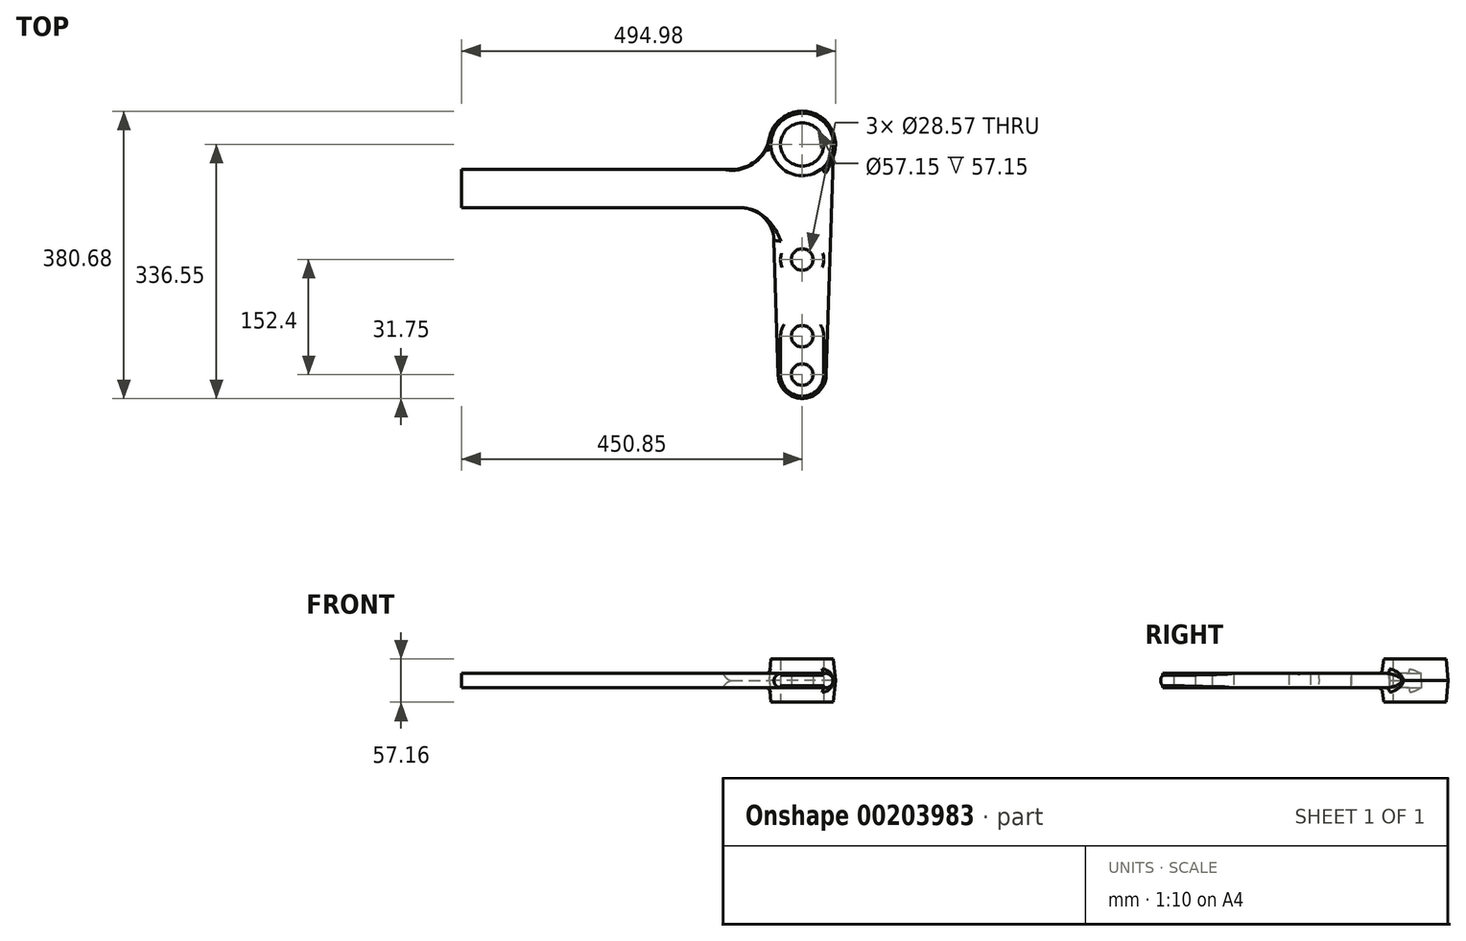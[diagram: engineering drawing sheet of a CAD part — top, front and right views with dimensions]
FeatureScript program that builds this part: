
annotation { "Feature Type Name" : "Feature", "Feature Type Description" : "" }
export const myFeature = defineFeature(function(context is Context, id is Id, definition is map)
    precondition{}
    {
        {
            var Q0;
            Q0=qCreatedBy(makeId("Top.planeOp"),FACE);
            var sketch = newSketch(context, id + "F0", { "sketchPlane" : qUnion([Q0])});
            skLineSegment(sketch, "E0", {"start": v(0, 0) * mm, "end": v(0, -304.8) * mm, "construction": true});
            skPoint(sketch, "E1", {"position": v(0, -254) * mm});
            skPoint(sketch, "E2", {"position": v(0, -152.4) * mm});
            skArc(sketch, "E3", {"start": v(-31.73, -305.8) * mm, "mid": v(0, -336.55) * mm, "end": v(31.73, -305.8) * mm});
            skLineSegment(sketch, "E4", {"start": v(-41.38, -1.31) * mm, "end": v(-31.73, -305.8) * mm});
            skLineSegment(sketch, "E5", {"start": v(41.38, -1.31) * mm, "end": v(31.73, -305.8) * mm});
            skCircle(sketch, "E6.converted", {"center": v(0, 0) * mm, "radius": 41.4 * mm});
            skArc(sketch, "E7", {"start": v(-28.58, -304.8) * mm, "mid": v(0, -333.38) * mm, "end": v(28.58, -304.8) * mm});
            skArc(sketch, "E8", {"start": v(28.58, -254) * mm, "mid": v(0, -225.42) * mm, "end": v(-28.57, -254) * mm});
            skCircle(sketch, "E9", {"center": v(0, -152.4) * mm, "radius": 28.58 * mm});
            skLineSegment(sketch, "E10", {"start": v(-28.57, -254) * mm, "end": v(-28.57, -304.8) * mm});
            skLineSegment(sketch, "E11", {"start": v(28.58, -254) * mm, "end": v(28.58, -304.8) * mm});
            skCircle(sketch, "E12", {"center": v(0, -304.8) * mm, "radius": 14.29 * mm});
            skCircle(sketch, "E13", {"center": v(0, -254) * mm, "radius": 14.29 * mm});
            skCircle(sketch, "E14", {"center": v(0, -152.4) * mm, "radius": 14.29 * mm});
            skCircle(sketch, "E15", {"center": v(0, 0) * mm, "radius": 28.58 * mm});
            skCircle(sketch, "E16.converted", {"center": v(0, 0) * mm, "radius": 44.45 * mm});
            skLineSegment(sketch, "E17", {"start": v(0, 0) * mm, "end": v(-450.85, -1.31) * mm, "construction": true});
            skLineSegment(sketch, "E18", {"start": v(-450.85, -33.06) * mm, "end": v(-40.38, -33.06) * mm});
            skLineSegment(sketch, "E19", {"start": v(-450.85, -83.86) * mm, "end": v(-38.77, -83.86) * mm});
            skLineSegment(sketch, "E20", {"start": v(-450.85, -1.31) * mm, "end": v(-450.85, -33.06) * mm, "construction": true});
            skLineSegment(sketch, "E21", {"start": v(-450.85, -33.06) * mm, "end": v(-450.85, -83.86) * mm});
            skArc(sketch, "E22", {"start": v(-93.58, -33.06) * mm, "mid": v(-61.18, -21.38) * mm, "end": v(-43.67, 8.28) * mm});
            skLineSegment(sketch, "E23", {"start": v(-43.67, 8.28) * mm, "end": v(-40.57, 8.28) * mm});
            skArc(sketch, "E24", {"start": v(-37.4, -126.9) * mm, "mid": v(-50.9, -96.39) * mm, "end": v(-81.83, -83.86) * mm});
            skSolve(sketch);
        }
        {
            var Q0;
            Q0=makeQuery(id+"F0.imprint","IMPRINT",FACE,{"disambiguationData":[TD([[makeQuery(id+"F0.imprint","IMPRINT",EDGE,{"derivedFrom":sQuery(id+"F0.wireOp",EDGE,"E3")}),1.0]])]});
            var Q1;
            {var subQ0=sQuery(id+"F0.wireOp",EDGE,"lDwGXFCf-zemv-MaXU-C33S-ghSfjxrpF6rd");Q1=makeQuery(id+"F0.imprint","IMPRINT",FACE,{"disambiguationData":[TD([[makeQuery(id+"F0.imprint","IMPRINT",EDGE,{"derivedFrom":subQ0}),1.0]])]});}
            var Q2;
            {var subQ0=sQuery(id+"F0.wireOp",EDGE,"E6.converted");var subQ1=sQuery(id+"F0.wireOp",EDGE,"E4");var subQ2=makeQuery(id+"F0.imprint","INTERSECT",VERTEX,{"derivedFrom":[subQ1,subQ0]});Q2=makeQuery(id+"F0.imprint","IMPRINT",FACE,{"disambiguationData":[TD([[makeQuery(id+"F0.imprint","IMPRINT",EDGE,{"disambiguationData":[TD([[subQ2,-1.0]])],"derivedFrom":subQ1}),1.0]])]});}
            extrude(context, id + "F1", {"entities" : qUnion([Q0, Q1, Q2]), "depth" : 9.52 * mm});
        }
        {
            var Q0;
            {var subQ5=sQuery(id+"F0.wireOp",EDGE,"E23");Q0=makeQuery(id+"F0.imprint","IMPRINT",FACE,{"disambiguationData":[TD([[makeQuery(id+"F0.imprint","IMPRINT",EDGE,{"derivedFrom":subQ5}),-1.0]])]});}
            var Q1;
            Q1=makeQuery(id+"F0.imprint","IMPRINT",FACE,{"disambiguationData":[TD([[makeQuery(id+"F0.imprint","IMPRINT",EDGE,{"derivedFrom":sQuery(id+"F0.wireOp",EDGE,"E18")}),-1.0]])]});
            var Q2;
            {var subQ5=sQuery(id+"F0.wireOp",EDGE,"E22");Q2=makeQuery(id+"F0.imprint","IMPRINT",FACE,{"disambiguationData":[TD([[makeQuery(id+"F0.imprint","IMPRINT",EDGE,{"derivedFrom":subQ5}),-1.0]])]});}
            extrude(context, id + "F2", {"entities" : qUnion([Q0, Q1, Q2]), "operationType" : NewBodyOperationType.ADD, "depth" : 9.52 * mm});
        }
        {
            var Q0;
            {var subQ0=sQuery(id+"F0.wireOp",EDGE,"lDwGXFCf-zemv-MaXU-C33S-ghSfjxrpF6rd");Q0=makeQuery(id+"F0.imprint","IMPRINT",FACE,{"disambiguationData":[TD([[makeQuery(id+"F0.imprint","IMPRINT",EDGE,{"derivedFrom":subQ0}),1.0]])]});}
            var Q1;
            Q1=makeQuery(id+"F0.imprint","IMPRINT",FACE,{"disambiguationData":[TD([[makeQuery(id+"F0.imprint","IMPRINT",EDGE,{"derivedFrom":sQuery(id+"F0.wireOp",EDGE,"E15")}),-1.0]])]});
            var Q2;
            {var subQ0=sQuery(id+"F0.wireOp",EDGE,"E6.converted");var subQ1=sQuery(id+"F0.wireOp",EDGE,"E4");var subQ2=makeQuery(id+"F0.imprint","INTERSECT",VERTEX,{"derivedFrom":[subQ1,subQ0]});Q2=makeQuery(id+"F0.imprint","IMPRINT",FACE,{"disambiguationData":[TD([[makeQuery(id+"F0.imprint","IMPRINT",EDGE,{"disambiguationData":[TD([[subQ2,-1.0]])],"derivedFrom":subQ1}),-1.0]])]});}
            var Q3;
            {var subQ0=sQuery(id+"F0.wireOp",EDGE,"E6.converted");var subQ1=sQuery(id+"F0.wireOp",EDGE,"E4");var subQ2=makeQuery(id+"F0.imprint","INTERSECT",VERTEX,{"derivedFrom":[subQ1,subQ0]});Q3=makeQuery(id+"F0.imprint","IMPRINT",FACE,{"disambiguationData":[TD([[makeQuery(id+"F0.imprint","IMPRINT",EDGE,{"disambiguationData":[TD([[subQ2,-1.0]])],"derivedFrom":subQ1}),1.0]])]});}
            var Q4;
            {var subQ5=sQuery(id+"F0.wireOp",EDGE,"E23");Q4=makeQuery(id+"F0.imprint","IMPRINT",FACE,{"disambiguationData":[TD([[makeQuery(id+"F0.imprint","IMPRINT",EDGE,{"derivedFrom":subQ5}),1.0]])]});}
            extrude(context, id + "F3", {"entities" : qUnion([Q0, Q1, Q2, Q3, Q4]), "depth" : 28.57 * mm});
        }
        {
            var Q0;
            Q0=makeQuery(id+"F3.opExtrude","CAP_EDGE",EDGE,{"disambiguationData":[OSD([sQuery(id+"F0.wireOp",EDGE,"E16.converted")])],"isStart":false});
            chamfer(context, id + "F4", {"entities" : qUnion([Q0]), "chamferType" : ChamferType.TWO_OFFSETS, "width1" : 3.17 * mm, "oppositeDirection" : false, "width2" : 31.75 * mm, "tangentPropagation" : true});
        }
        {
            var Q0;
            Q0=makeQuery(id+"F1.opExtrude","SWEPT_BODY",BODY,{"disambiguationData":[OSD([sQuery(id+"F0.wireOp",EDGE,"E3"),sQuery(id+"F0.wireOp",EDGE,"E4"),sQuery(id+"F0.wireOp",EDGE,"E5"),sQuery(id+"F0.wireOp",EDGE,"E6.converted"),sQuery(id+"F0.wireOp",EDGE,"E7"),sQuery(id+"F0.wireOp",EDGE,"E8"),sQuery(id+"F0.wireOp",EDGE,"E9"),sQuery(id+"F0.wireOp",EDGE,"E10"),sQuery(id+"F0.wireOp",EDGE,"E11")])]});
            var Q1;
            Q1=makeQuery(id+"F3.opExtrude","SWEPT_BODY",BODY,{"disambiguationData":[OSD([sQuery(id+"F0.wireOp",EDGE,"E15"),sQuery(id+"F0.wireOp",EDGE,"E16.converted")])]});
            booleanBodies(context, id + "F5", {"operationType" : BooleanOperationType.UNION, "tools" : qUnion([Q0, Q1])});
        }
        {
            var Q0;
            {var subQ1=sQuery(id+"F0.wireOp",EDGE,"E4");var subQ2=sQuery(id+"F0.wireOp",EDGE,"E3");Q0=makeQuery(id+"F2.boolean.opBoolean","SPLIT",EDGE,{"disambiguationData":[TD([makeQuery(id+"F1.opExtrude","SWEPT_FACE",FACE,{"disambiguationData":[OSD([subQ2])]})])],"derivedFrom":makeQuery(id+"F1.opExtrude","CAP_EDGE",EDGE,{"disambiguationData":[OSD([subQ1])],"isStart":false})});}
            fillet(context, id + "F6", {"entities" : qUnion([Q0]), "radius" : 9.52 * mm, "tangentPropagation" : true, "allowEdgeOverflow" : false});
        }
        {
            var Q0;
            Q0=makeQuery(id+"F6.opFillet","BLEND_EDGE",EDGE,{"blendedFrom":[makeQuery(id+"F1.opExtrude","CAP_EDGE",EDGE,{"disambiguationData":[OSD([sQuery(id+"F0.wireOp",EDGE,"E4")])],"isStart":false}),makeQuery(id+"F2.opExtrude","SWEPT_FACE",FACE,{"disambiguationData":[OSD([sQuery(id+"F0.wireOp",EDGE,"E19")])]})],"blendedInto":[makeQuery(id+"F2.opExtrude","SWEPT_FACE",FACE,{"disambiguationData":[OSD([sQuery(id+"F0.wireOp",EDGE,"E19")])]})]});
            fillet(context, id + "F7", {"entities" : qUnion([Q0]), "radius" : 44.45 * mm, "tangentPropagation" : true, "allowEdgeOverflow" : false});
        }
        {
            var Q0;
            Q0=makeQuery(id+"F2.opExtrude","CAP_EDGE",EDGE,{"disambiguationData":[OSD([sQuery(id+"F0.wireOp",EDGE,"E22")])],"isStart":false});
            chamfer(context, id + "F8", {"entities" : qUnion([Q0]), "chamferType" : ChamferType.TWO_OFFSETS, "width1" : 9.52 * mm, "oppositeDirection" : false, "width2" : 1.27 * mm});
        }
        {
            var Q0;
            {var subQ0=sQuery(id+"F0.wireOp",EDGE,"E9");var subQ1=sQuery(id+"F0.wireOp",EDGE,"E11");var subQ2=sQuery(id+"F0.wireOp",EDGE,"E10");var subQ3=sQuery(id+"F0.wireOp",EDGE,"E8");var subQ4=sQuery(id+"F0.wireOp",EDGE,"E7");var subQ5=sQuery(id+"F0.wireOp",EDGE,"E6.converted");var subQ6=sQuery(id+"F0.wireOp",EDGE,"E4");var subQ7=makeQuery(id+"F2.boolean.opBoolean","MERGE",FACE,{"derivedFrom":[makeQuery(id+"F1.opExtrude","CAP_FACE",FACE,{"disambiguationData":[OSD([sQuery(id+"F0.wireOp",EDGE,"E3"),subQ6,sQuery(id+"F0.wireOp",EDGE,"E5"),subQ5,subQ4,subQ3,subQ0,subQ2,subQ1])],"isStart":true}),makeQuery(id+"F2.opExtrude","CAP_FACE",FACE,{"disambiguationData":[OSD([subQ6,subQ5,sQuery(id+"F0.wireOp",EDGE,"E18"),sQuery(id+"F0.wireOp",EDGE,"E19"),sQuery(id+"F0.wireOp",EDGE,"E21"),sQuery(id+"F0.wireOp",EDGE,"E22"),sQuery(id+"F0.wireOp",EDGE,"E23"),sQuery(id+"F0.wireOp",EDGE,"E24")])],"isStart":true})]});Q0=makeQuery(id+"F5.opBoolean","INTERSECT",EDGE,{"derivedFrom":[makeQuery(id+"F11.boolean.opBoolean","MERGE",FACE,{"derivedFrom":[makeQuery(id+"Fc0r55Mq1ALnL4g_1.opFillet","SPLIT",FACE,{"disambiguationData":[OD(0.0)],"derivedFrom":subQ7}),makeQuery(id+"Fc0r55Mq1ALnL4g_1.opFillet","SPLIT",FACE,{"disambiguationData":[OD(1.0)],"derivedFrom":subQ7}),makeQuery(id+"F11.opExtrude","CAP_FACE",FACE,{"disambiguationData":[OSD([subQ4,subQ3,subQ2,subQ1,sQuery(id+"F0.wireOp",EDGE,"E12"),sQuery(id+"F0.wireOp",EDGE,"E13")])],"isStart":true}),makeQuery(id+"F11.opExtrude","CAP_FACE",FACE,{"disambiguationData":[OSD([subQ0,sQuery(id+"F0.wireOp",EDGE,"E14")])],"isStart":true})]}),makeQuery(id+"F10.opPattern","COPY",FACE,{"derivedFrom":makeQuery(id+"F4.opChamfer","BLEND_FACE",FACE,{"disambiguationData":[OSD([sQuery(id+"F0.wireOp",EDGE,"E16.converted")])]}),"instanceName":"1"})]});}
            var Q1;
            {var subQ0=sQuery(id+"F0.wireOp",EDGE,"E9");var subQ1=sQuery(id+"F0.wireOp",EDGE,"E11");var subQ2=sQuery(id+"F0.wireOp",EDGE,"E10");var subQ3=sQuery(id+"F0.wireOp",EDGE,"E8");var subQ4=sQuery(id+"F0.wireOp",EDGE,"E7");var subQ5=sQuery(id+"F0.wireOp",EDGE,"E6.converted");var subQ6=sQuery(id+"F0.wireOp",EDGE,"E4");var subQ7=makeQuery(id+"F2.boolean.opBoolean","MERGE",FACE,{"derivedFrom":[makeQuery(id+"F1.opExtrude","CAP_FACE",FACE,{"disambiguationData":[OSD([sQuery(id+"F0.wireOp",EDGE,"E3"),subQ6,sQuery(id+"F0.wireOp",EDGE,"E5"),subQ5,subQ4,subQ3,subQ0,subQ2,subQ1])],"isStart":false}),makeQuery(id+"F2.opExtrude","CAP_FACE",FACE,{"disambiguationData":[OSD([subQ6,subQ5,sQuery(id+"F0.wireOp",EDGE,"E18"),sQuery(id+"F0.wireOp",EDGE,"E19"),sQuery(id+"F0.wireOp",EDGE,"E21"),sQuery(id+"F0.wireOp",EDGE,"E22"),sQuery(id+"F0.wireOp",EDGE,"E23"),sQuery(id+"F0.wireOp",EDGE,"E24")])],"isStart":false})]});Q1=makeQuery(id+"F5.opBoolean","INTERSECT",EDGE,{"derivedFrom":[makeQuery(id+"F11.boolean.opBoolean","MERGE",FACE,{"derivedFrom":[makeQuery(id+"Fc0r55Mq1ALnL4g_1.opFillet","SPLIT",FACE,{"disambiguationData":[OD(0.0)],"derivedFrom":subQ7}),makeQuery(id+"Fc0r55Mq1ALnL4g_1.opFillet","SPLIT",FACE,{"disambiguationData":[OD(1.0)],"derivedFrom":subQ7}),makeQuery(id+"F11.opExtrude","CAP_FACE",FACE,{"disambiguationData":[OSD([subQ4,subQ3,subQ2,subQ1,sQuery(id+"F0.wireOp",EDGE,"E12"),sQuery(id+"F0.wireOp",EDGE,"E13")])],"isStart":false}),makeQuery(id+"F11.opExtrude","CAP_FACE",FACE,{"disambiguationData":[OSD([subQ0,sQuery(id+"F0.wireOp",EDGE,"E14")])],"isStart":false})]}),makeQuery(id+"F4.opChamfer","BLEND_FACE",FACE,{"disambiguationData":[OSD([sQuery(id+"F0.wireOp",EDGE,"E16.converted")])]})]});}
            fillet(context, id + "F9", {"entities" : qUnion([Q0, Q1]), "radius" : 6.35 * mm, "tangentPropagation" : true, "allowEdgeOverflow" : false});
        }
        {
            var Q0;
            Q0=makeQuery(id+"F1.opExtrude","SWEPT_BODY",BODY,{"disambiguationData":[OSD([sQuery(id+"F0.wireOp",EDGE,"E3"),sQuery(id+"F0.wireOp",EDGE,"E4"),sQuery(id+"F0.wireOp",EDGE,"E5"),sQuery(id+"F0.wireOp",EDGE,"E6.converted"),sQuery(id+"F0.wireOp",EDGE,"E7"),sQuery(id+"F0.wireOp",EDGE,"E8"),sQuery(id+"F0.wireOp",EDGE,"E9"),sQuery(id+"F0.wireOp",EDGE,"E10"),sQuery(id+"F0.wireOp",EDGE,"E11")])]});
            var Q1;
            Q1=qCreatedBy(makeId("Top.planeOp"),FACE);
            mirror(context, id + "F10", {"operationType" : NewBodyOperationType.ADD, "entities" : qUnion([Q0]), "mirrorPlane" : qUnion([Q1])});
        }
        {
            var Q0;
            Q0=makeQuery(id+"F0.imprint","IMPRINT",FACE,{"disambiguationData":[TD([[makeQuery(id+"F0.imprint","IMPRINT",EDGE,{"derivedFrom":sQuery(id+"F0.wireOp",EDGE,"E9")}),1.0]])]});
            var Q1;
            Q1=makeQuery(id+"F0.imprint","IMPRINT",FACE,{"disambiguationData":[TD([[makeQuery(id+"F0.imprint","IMPRINT",EDGE,{"derivedFrom":sQuery(id+"F0.wireOp",EDGE,"E7")}),1.0]])]});
            extrude(context, id + "F11", {"entities" : qUnion([Q0, Q1]), "operationType" : NewBodyOperationType.ADD, "endBound" : BoundingType.SYMMETRIC, "depth" : 19.05 * mm});
        }
    });
